# Revit family: RBA4150-102
name_source: partatom
category: Plumbing Fixtures
units: mm (PartAtom-declared; Revit-internal decimal feet)

## family parameters
Always vertical = Yes
Cut with Voids When Loaded = No
Part Type = Normal
Room Calculation Point = No
Round Connector Dimension = Use Diameter
Shared = No
Work Plane-Based = No

## types (3) — shared parameters
CW Connection = Yes
HW Connection = Yes
Manufacturer = RBA Group
Vent Connection = Yes
Waste Connection = Yes
zero-valued in all types: Default Elevation

## per-type parameters (varying)
| type | Description | Materials and Finishes | Model | Modified Issue | URL |
| RBA4150- | Raffaello Shower T-Rail | Stainless Steel / White Antibacterial Finish | RBA4601-061 | 20180813.01 | http://www.rba.com.au |
| RBA4150-102 | Accessible Compliant Backrest, with Matte Black rails | Stainless Steel / Matte Black Antibacterial Finish | RBA4150-102 | 20190315.01 | www.rba.com.au |
| RBA4150-- | Raffaello Shower T-Rail | Stainless Steel / Bright Finish | RBA4601-069 | 20180813.01 | http://www.rba.com.au |

## geometry (parser evidence)
native form markers: Blend x4, Sweep x3
no freeform markers — native parametric forms only
